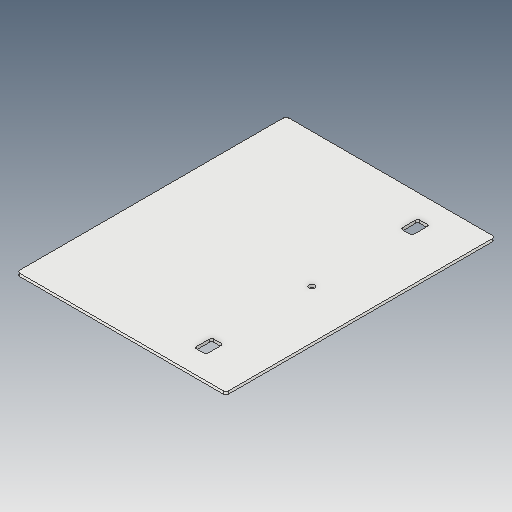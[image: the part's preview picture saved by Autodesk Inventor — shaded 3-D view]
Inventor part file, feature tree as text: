
AUTODESK INVENTOR PART (.ipt)
format: ipt  version: 2023.5 (Build 275446000, 446)  size: 98,304 bytes
history: native  units: in
note: dims shown in document units (in); Inventor stores cm internally (conversion verified against a paired STEP export)
features: fillet x1
ambient origin geometry x8: Origin, YZ Plane, XZ Plane, XY Plane, X Axis, Y Axis, Z Axis, Center Point
bodies: Solid1 (feature_tree)
feature tree (1):
  fillet  "Fillet2"  [1 undecoded]
note: 1 required parameter value undecoded (feature->parameter linkage not recoverable at this tier; creation-order binding heuristic only, values carry confidence <= 0.55)
